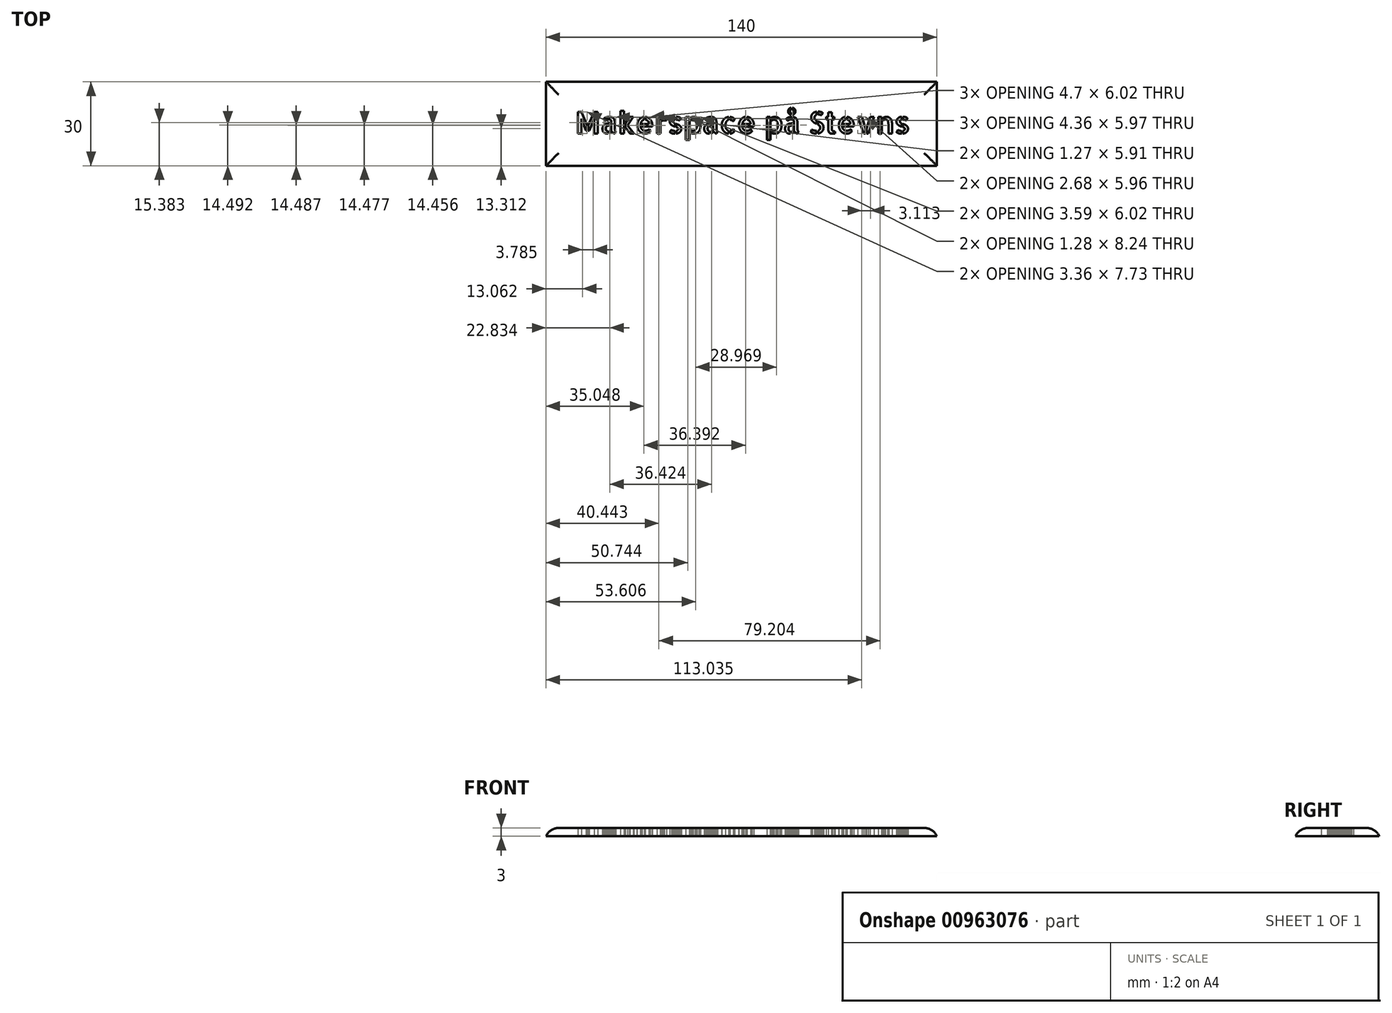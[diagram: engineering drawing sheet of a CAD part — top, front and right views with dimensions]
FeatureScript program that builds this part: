
annotation { "Feature Type Name" : "Feature", "Feature Type Description" : "" }
export const myFeature = defineFeature(function(context is Context, id is Id, definition is map)
    precondition{}
    {
        {
            var Q0;
            Q0=qCreatedBy(makeId("Top.planeOp"),FACE);
            var sketch = newSketch(context, id + "F0", { "sketchPlane" : qUnion([Q0])});
            skLineSegment(sketch, "E0.bottom", {"start": v(-68.53, 13.48) * mm, "end": v(61.47, 13.48) * mm});
            skLineSegment(sketch, "E0.top", {"start": v(-68.53, -6.52) * mm, "end": v(61.47, -6.52) * mm});
            skLineSegment(sketch, "E0.left", {"start": v(-68.53, 13.48) * mm, "end": v(-68.53, -6.52) * mm});
            skLineSegment(sketch, "E0.right", {"start": v(61.47, 13.48) * mm, "end": v(61.47, -6.52) * mm});
            skLineSegment(sketch, "E1.0", {"start": v(-73.53, -11.52) * mm, "end": v(66.47, -11.52) * mm});
            skLineSegment(sketch, "E1.1", {"start": v(-73.53, 18.48) * mm, "end": v(-73.53, -11.52) * mm});
            skLineSegment(sketch, "E1.2", {"start": v(-73.53, 18.48) * mm, "end": v(66.47, 18.48) * mm});
            skLineSegment(sketch, "E1.3", {"start": v(66.47, 18.48) * mm, "end": v(66.47, -11.52) * mm});
            skText(sketch, "E2", { "text": "Makerspace på Stevns", "fontName": "AllertaStencil-Regular.ttf"});
            skPoint(sketch, "E3", {"position": v(-65.61, 10.92) * mm});
            skPoint(sketch, "E4", {"position": v(59.2, 10.92) * mm});
            const initialGuessF0  = {"E2": [-0.06311, 0, 1, 0, 0.00773]};
            skSetInitialGuess(sketch, initialGuessF0);
            skSolve(sketch);
        }
        {
            var Q0;
            Q0=makeQuery(id+"F0.imprint","IMPRINT",FACE,{"disambiguationData":[TD([[makeQuery(id+"F0.imprint","IMPRINT",EDGE,{"derivedFrom":sQuery(id+"F0.wireOp",EDGE,"E0.bottom")}),-1.0]])]});
            var Q1;
            Q1=makeQuery(id+"F0.imprint","IMPRINT",FACE,{"disambiguationData":[TD([[makeQuery(id+"F0.imprint","IMPRINT",EDGE,{"derivedFrom":sQuery(id+"F0.wireOp",EDGE,"E0.bottom")}),1.0]])]});
            extrude(context, id + "F1", {"entities" : qUnion([Q0, Q1]), "depth" : 3 * mm, "offsetDistance" : 25 * mm});
        }
        {
            var Q0;
            Q0=makeQuery(id+"F1.opExtrude","CAP_EDGE",EDGE,{"disambiguationData":[OSD([sQuery(id+"F0.wireOp",EDGE,"E1.0")])],"isStart":false});
            var Q1;
            Q1=makeQuery(id+"F1.opExtrude","CAP_EDGE",EDGE,{"disambiguationData":[OSD([sQuery(id+"F0.wireOp",EDGE,"E1.3")])],"isStart":false});
            var Q2;
            Q2=makeQuery(id+"F1.opExtrude","CAP_EDGE",EDGE,{"disambiguationData":[OSD([sQuery(id+"F0.wireOp",EDGE,"E1.2")])],"isStart":false});
            var Q3;
            Q3=makeQuery(id+"F1.opExtrude","CAP_EDGE",EDGE,{"disambiguationData":[OSD([sQuery(id+"F0.wireOp",EDGE,"E1.1")])],"isStart":false});
            fillet(context, id + "F2", {"entities" : qUnion([Q0, Q1, Q2, Q3]), "radius" : 5 * mm, "tangentPropagation" : true, "allowEdgeOverflow" : false});
        }
    });
